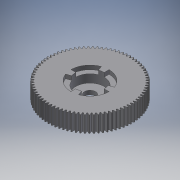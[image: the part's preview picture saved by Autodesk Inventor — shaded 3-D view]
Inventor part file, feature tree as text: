
AUTODESK INVENTOR PART (.ipt)
format: ipt  version: 2017 (Build 210142000, 142)  size: 477,696 bytes
history: native  units: mm
features: extrude x5, sketch x4, pattern_circular x2
ambient origin geometry x8: Origin, YZ Plane, XZ Plane, XY Plane, X Axis, Y Axis, Z Axis, Center Point
bodies: Solid1 (feature_tree)
feature tree (11):
  sketch  "Sketch1"  dims[d0=20.0mm d1=0.0mm]
  extrude  "Extrusion1"  TaperAngle=0.0deg  [1 undecoded]
  extrude  "Extrusion2"  Depth=10.0mm TaperAngle=360.0deg
  pattern_circular  "Circular Pattern1"  [2 undecoded]
  extrude  "Extrusion3"  Depth=15.0mm TaperAngle=0.0deg
  extrude  "Extrusion4"  Depth=5.0mm
  extrude  "Extrusion5"  Depth=5.0mm
  pattern_circular  "Circular Pattern2"  [2 undecoded]
  sketch  "Sketch2"  dims[d2=10.0mm d3=0.0mm d4=810.0mm d5=360.0deg]
  sketch  "Sketch3"  dims[d7=13.5mm]
  sketch  "Sketch4"  dims[d8=10.0mm d9=0.0mm d10=35.0mm d11=15.0mm d12=0.0mm d13=6.0mm d14=12.217305mm d15=5.0mm d16=0.0mm d17=40.0mm d18=360.0deg]
note: 5 required parameter values undecoded (feature->parameter linkage not recoverable at this tier; creation-order binding heuristic only, values carry confidence <= 0.55)
